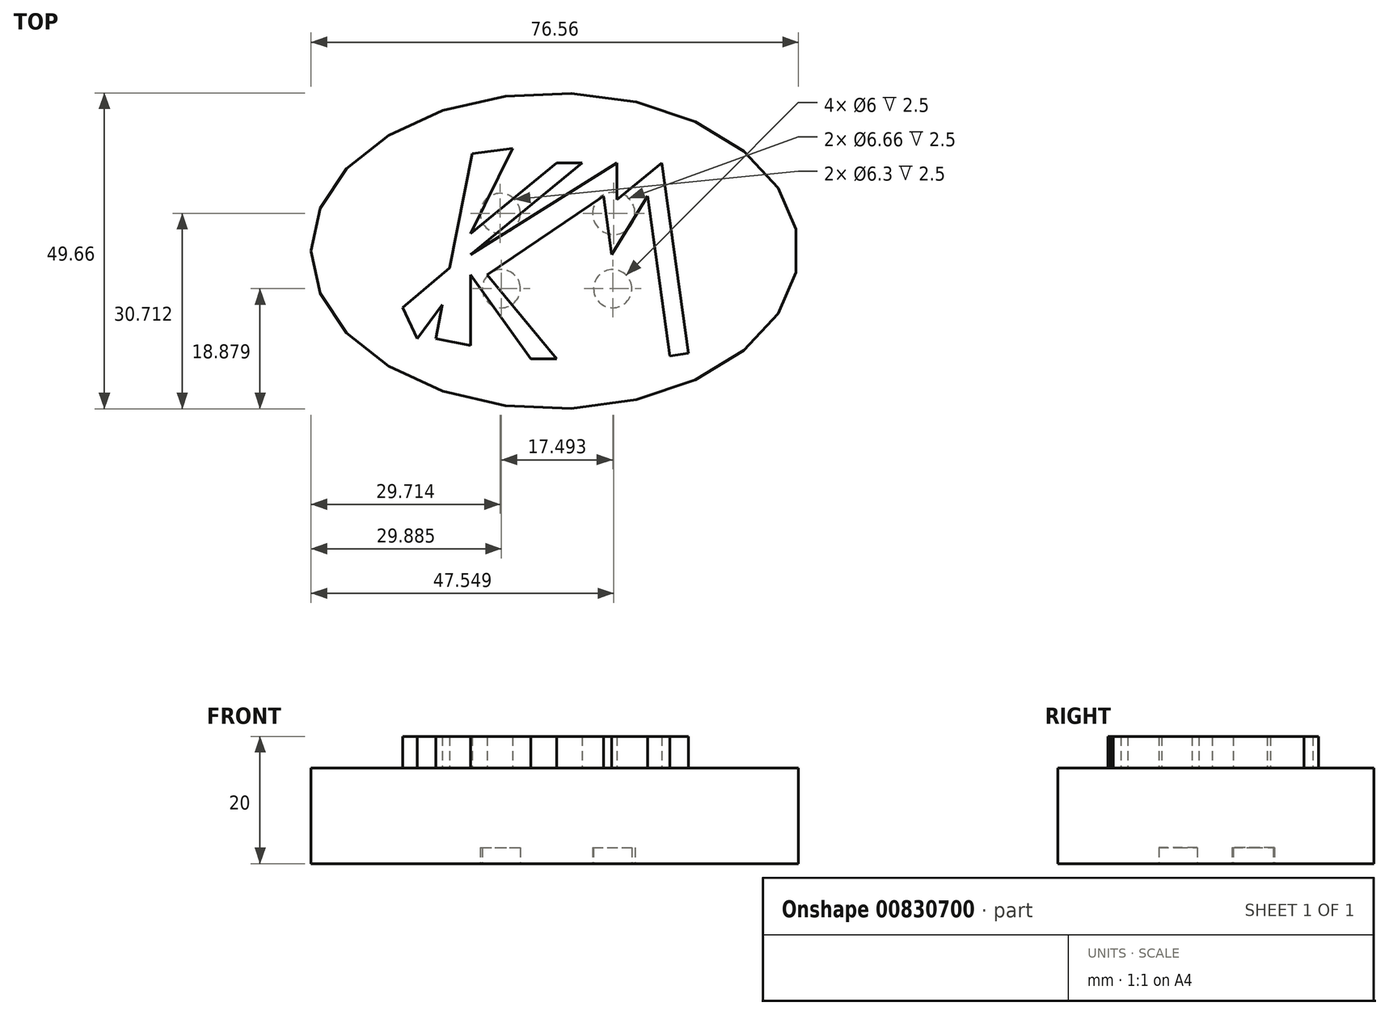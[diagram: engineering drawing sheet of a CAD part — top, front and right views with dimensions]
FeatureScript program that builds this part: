
annotation { "Feature Type Name" : "Feature", "Feature Type Description" : "" }
export const myFeature = defineFeature(function(context is Context, id is Id, definition is map)
    precondition{}
    {
        {
            var Q0;
            Q0=qCreatedBy(makeId("Top.planeOp"),FACE);
            var sketch = newSketch(context, id + "F0", { "sketchPlane" : qUnion([Q0])});
            skEllipse(sketch, "E0", {"center": v(-29.79, 27.2) * mm, "majorRadius": 38.28 * mm, "minorRadius": 24.83 * mm, "majorAxis": v(-1, 0)});
            skSolve(sketch);
        }
        {
            var Q0;
            Q0=makeQuery(id+"F0.imprint","IMPRINT",FACE,{"disambiguationData":[TD([[makeQuery(id+"F0.imprint","IMPRINT",EDGE,{"derivedFrom":sQuery(id+"F0.wireOp",EDGE,"E0")}),1.0]])]});
            var sketch = newSketch(context, id + "F1", { "sketchPlane" : qUnion([Q0])});
            skSolve(sketch);
        }
        {
            var Q0;
            Q0=makeQuery(id+"F1.imprint","IMPRINT",FACE,{"disambiguationData":[TD([[makeQuery(id+"F1.imprint","IMPRINT",EDGE,{"derivedFrom":makeQuery(id+"F0.imprint","IMPRINT",EDGE,{"derivedFrom":sQuery(id+"F0.wireOp",EDGE,"E0")})}),1.0]])]});
            var Q1;
            Q1=makeQuery(id+"F0.imprint","IMPRINT",FACE,{"disambiguationData":[TD([[makeQuery(id+"F0.imprint","IMPRINT",EDGE,{"derivedFrom":sQuery(id+"F0.wireOp",EDGE,"E0")}),1.0]])]});
            extrude(context, id + "F2", {"entities" : qUnion([Q0, Q1]), "depth" : 15 * mm, "offsetDistance" : 25.4 * mm});
        }
        {
            var Q0;
            {var subQ0=sQuery(id+"F0.wireOp",EDGE,"E0");Q0=makeQuery(id+"F2.opExtrude","CAP_FACE",FACE,{"disambiguationData":[OSD([subQ0]),TDD([makeQuery(id+"F0.imprint","IMPRINT",EDGE,{"derivedFrom":subQ0})])],"isStart":false});}
            var sketch = newSketch(context, id + "F3", { "sketchPlane" : qUnion([Q0])});
            skLineSegment(sketch, "E1", {"start": v(-42.74, 42.45) * mm, "end": v(-48.5, 13.38) * mm});
            skLineSegment(sketch, "E2", {"start": v(-48.5, 13.38) * mm, "end": v(-43.01, 12.3) * mm});
            skLineSegment(sketch, "E3", {"start": v(-43.01, 12.3) * mm, "end": v(-43.01, 23.46) * mm});
            skLineSegment(sketch, "E4", {"start": v(-43.01, 23.46) * mm, "end": v(-33.53, 10.22) * mm});
            skLineSegment(sketch, "E5", {"start": v(-33.53, 10.22) * mm, "end": v(-29.5, 10.22) * mm});
            skLineSegment(sketch, "E6", {"start": v(-29.5, 10.22) * mm, "end": v(-43.01, 26.62) * mm});
            skLineSegment(sketch, "E7", {"start": v(-43.01, 26.62) * mm, "end": v(-25.5, 41.05) * mm});
            skLineSegment(sketch, "E8", {"start": v(-25.5, 41.05) * mm, "end": v(-29.5, 41.05) * mm});
            skLineSegment(sketch, "E9", {"start": v(-29.5, 41.05) * mm, "end": v(-43.01, 29.92) * mm});
            skLineSegment(sketch, "E10", {"start": v(-43.01, 29.92) * mm, "end": v(-36.4, 43.31) * mm});
            skLineSegment(sketch, "E11", {"start": v(-36.4, 43.31) * mm, "end": v(-42.74, 42.45) * mm});
            skLineSegment(sketch, "E12", {"start": v(-53.68, 18.28) * mm, "end": v(-51.37, 13.38) * mm});
            skLineSegment(sketch, "E13", {"start": v(-51.37, 13.38) * mm, "end": v(-47.44, 18.7) * mm});
            skLineSegment(sketch, "E14", {"start": v(-53.68, 18.28) * mm, "end": v(-46.3, 24.51) * mm});
            skLineSegment(sketch, "E15", {"start": v(-46.3, 24.51) * mm, "end": v(-47.44, 18.7) * mm});
            skLineSegment(sketch, "E16", {"start": v(-43.01, 26.62) * mm, "end": v(-20, 41.05) * mm});
            skLineSegment(sketch, "E17", {"start": v(-20, 41.05) * mm, "end": v(-20, 35.26) * mm});
            skLineSegment(sketch, "E18", {"start": v(-20, 35.26) * mm, "end": v(-12.97, 41.05) * mm});
            skLineSegment(sketch, "E19", {"start": v(-12.97, 41.05) * mm, "end": v(-8.78, 11.08) * mm});
            skLineSegment(sketch, "E20", {"start": v(-8.78, 11.08) * mm, "end": v(-11.68, 10.67) * mm});
            skLineSegment(sketch, "E21", {"start": v(-11.68, 10.67) * mm, "end": v(-15.2, 35.78) * mm});
            skLineSegment(sketch, "E22", {"start": v(-15.2, 35.78) * mm, "end": v(-20.87, 26.62) * mm});
            skLineSegment(sketch, "E23", {"start": v(-20.87, 26.62) * mm, "end": v(-22.15, 35.78) * mm});
            skLineSegment(sketch, "E24", {"start": v(-22.15, 35.78) * mm, "end": v(-40.4, 23.46) * mm});
            skLineSegment(sketch, "E25", {"start": v(-40.4, 23.46) * mm, "end": v(-43.01, 26.62) * mm});
            skSolve(sketch);
        }
        {
            var Q0;
            {var subQ3=sQuery(id+"F3.wireOp",EDGE,"E2");Q0=makeQuery(id+"F3.imprint","IMPRINT",FACE,{"disambiguationData":[TD([[makeQuery(id+"F3.imprint","IMPRINT",EDGE,{"derivedFrom":subQ3}),1.0]])]});}
            var Q1;
            Q1=makeQuery(id+"F3.imprint","IMPRINT",FACE,{"disambiguationData":[TD([[makeQuery(id+"F3.imprint","IMPRINT",EDGE,{"derivedFrom":sQuery(id+"F3.wireOp",EDGE,"E16")}),-1.0]])]});
            var Q2;
            Q2=makeQuery(id+"F3.imprint","IMPRINT",FACE,{"disambiguationData":[TD([[makeQuery(id+"F3.imprint","IMPRINT",EDGE,{"derivedFrom":sQuery(id+"F3.wireOp",EDGE,"E12")}),1.0]])]});
            extrude(context, id + "F4", {"entities" : qUnion([Q0, Q1, Q2]), "depth" : 5 * mm, "offsetDistance" : 25.4 * mm});
        }
        {
            var Q0;
            {var subQ0=sQuery(id+"F0.wireOp",EDGE,"E0");Q0=makeQuery(id+"F2.opExtrude","CAP_FACE",FACE,{"disambiguationData":[OSD([subQ0]),TDD([makeQuery(id+"F0.imprint","IMPRINT",EDGE,{"derivedFrom":subQ0})])],"isStart":true});}
            var sketch = newSketch(context, id + "F5", { "sketchPlane" : qUnion([Q0])});
            skLineSegment(sketch, "E26", {"start": v(-68.07, -27.2) * mm, "end": v(8.5, -27.2) * mm});
            skLineSegment(sketch, "E27", {"start": v(-29.79, -2.37) * mm, "end": v(-29.79, -52.03) * mm});
            skPoint(sketch, "E28", {"position": v(-44.47, -37.27) * mm});
            skPoint(sketch, "E29.MirrorP", {"position": v(-44.47, -17.12) * mm});
            skPoint(sketch, "E30.MirrorP", {"position": v(-15.1, -17.12) * mm});
            skPoint(sketch, "E31.MirrorP", {"position": v(-15.1, -37.27) * mm});
            skSolve(sketch);
        }
        {
            var Q0;
            {var subQ0=sQuery(id+"F5.wireOp",EDGE,"E26");var subQ4=sQuery(id+"F5.wireOp",EDGE,"E27");var subQ5=makeQuery(id+"F5.imprint","INTERSECT",VERTEX,{"derivedFrom":[subQ0,subQ4]});Q0=makeQuery(id+"F5.imprint","IMPRINT",FACE,{"disambiguationData":[TD([[makeQuery(id+"F5.imprint","IMPRINT",EDGE,{"disambiguationData":[TD([[subQ5,1.0]])],"derivedFrom":subQ0}),1.0]])]});}
            var sketch = newSketch(context, id + "F6", { "sketchPlane" : qUnion([Q0])});
            skCircle(sketch, "E32", {"center": v(-38.18, -21.25) * mm, "radius": 3 * mm});
            skCircle(sketch, "E33", {"center": v(-20.7, -21.25) * mm, "radius": 3 * mm});
            skCircle(sketch, "E34", {"center": v(-38.36, -33.08) * mm, "radius": 3.15 * mm});
            skCircle(sketch, "E35", {"center": v(-20.52, -33.08) * mm, "radius": 3.33 * mm});
            skSolve(sketch);
        }
        {
            var Q0;
            Q0=makeQuery(id+"F6.imprint","IMPRINT",FACE,{"disambiguationData":[TD([[makeQuery(id+"F6.imprint","IMPRINT",EDGE,{"derivedFrom":sQuery(id+"F6.wireOp",EDGE,"E32")}),1.0]])]});
            var Q1;
            Q1=makeQuery(id+"F6.imprint","IMPRINT",FACE,{"disambiguationData":[TD([[makeQuery(id+"F6.imprint","IMPRINT",EDGE,{"derivedFrom":sQuery(id+"F6.wireOp",EDGE,"E33")}),1.0]])]});
            var Q2;
            Q2=makeQuery(id+"F6.imprint","IMPRINT",FACE,{"disambiguationData":[TD([[makeQuery(id+"F6.imprint","IMPRINT",EDGE,{"derivedFrom":sQuery(id+"F6.wireOp",EDGE,"E35")}),1.0]])]});
            var Q3;
            Q3=makeQuery(id+"F6.imprint","IMPRINT",FACE,{"disambiguationData":[TD([[makeQuery(id+"F6.imprint","IMPRINT",EDGE,{"derivedFrom":sQuery(id+"F6.wireOp",EDGE,"E34")}),1.0]])]});
            extrude(context, id + "F7", {"entities" : qUnion([Q0, Q1, Q2, Q3]), "operationType" : NewBodyOperationType.REMOVE, "oppositeDirection" : true, "depth" : 2.5 * mm, "offsetDistance" : 25.4 * mm});
        }
    });
